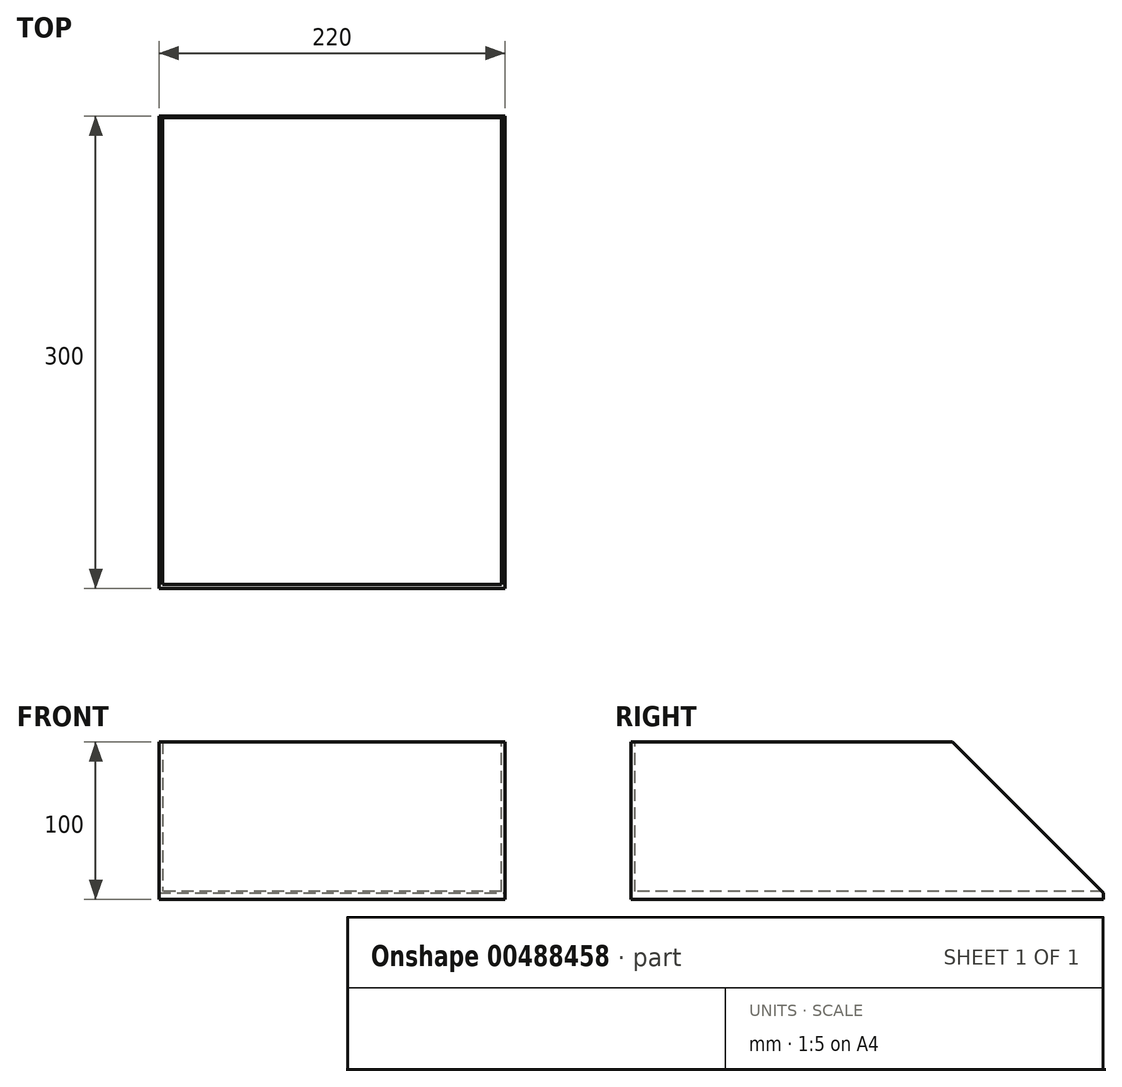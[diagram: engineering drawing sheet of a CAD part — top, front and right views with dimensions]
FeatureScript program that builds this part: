
annotation { "Feature Type Name" : "Feature", "Feature Type Description" : "" }
export const myFeature = defineFeature(function(context is Context, id is Id, definition is map)
    precondition{}
    {
        {
            var Q0;
            Q0=qCreatedBy(makeId("Top.planeOp"),FACE);
            var sketch = newSketch(context, id + "F0", { "sketchPlane" : qUnion([Q0])});
            skLineSegment(sketch, "E0.bottom", {"start": v(-110, 150) * mm, "end": v(110, 150) * mm});
            skLineSegment(sketch, "E0.top", {"start": v(-110, -150) * mm, "end": v(110, -150) * mm});
            skLineSegment(sketch, "E0.left", {"start": v(-110, 150) * mm, "end": v(-110, -150) * mm});
            skLineSegment(sketch, "E0.right", {"start": v(110, 150) * mm, "end": v(110, -150) * mm});
            skPoint(sketch, "E0.middle", {"position": v(0, 0) * mm});
            skSolve(sketch);
        }
        {
            var Q0;
            Q0=makeQuery(id+"F0.imprint","IMPRINT",FACE,{"disambiguationData":[TD([[makeQuery(id+"F0.imprint","IMPRINT",EDGE,{"derivedFrom":sQuery(id+"F0.wireOp",EDGE,"E0.bottom")}),-1.0]])]});
            extrude(context, id + "F1", {"entities" : qUnion([Q0]), "depth" : 100 * mm});
        }
        {
            var Q0;
            Q0=makeQuery(id+"F1.opExtrude","CAP_FACE",FACE,{"disambiguationData":[OSD([sQuery(id+"F0.wireOp",EDGE,"E0.bottom"),sQuery(id+"F0.wireOp",EDGE,"E0.top"),sQuery(id+"F0.wireOp",EDGE,"E0.left"),sQuery(id+"F0.wireOp",EDGE,"E0.right")])],"isStart":false});
            var sketch = newSketch(context, id + "F2", { "sketchPlane" : qUnion([Q0])});
            skLineSegment(sketch, "E1.bottom", {"start": v(107.5, 147.5) * mm, "end": v(-107.5, 147.5) * mm});
            skLineSegment(sketch, "E1.top", {"start": v(107.5, -147.5) * mm, "end": v(-107.5, -147.5) * mm});
            skLineSegment(sketch, "E1.left", {"start": v(107.5, 147.5) * mm, "end": v(107.5, -147.5) * mm});
            skLineSegment(sketch, "E1.right", {"start": v(-107.5, 147.5) * mm, "end": v(-107.5, -147.5) * mm});
            skPoint(sketch, "E1.middle", {"position": v(0, 0) * mm});
            skSolve(sketch);
        }
        {
            var Q0;
            Q0=makeQuery(id+"F2.imprint","IMPRINT",FACE,{"disambiguationData":[TD([[makeQuery(id+"F2.imprint","IMPRINT",EDGE,{"derivedFrom":sQuery(id+"F2.wireOp",EDGE,"E1.bottom")}),1.0]])]});
            extrude(context, id + "F3", {"entities" : qUnion([Q0]), "operationType" : NewBodyOperationType.REMOVE, "oppositeDirection" : true, "depth" : 95 * mm});
        }
        {
            var Q0;
            Q0=makeQuery(id+"F3.boolean.opBoolean","COPY",FACE,{"derivedFrom":makeQuery(id+"F3.opExtrude","SWEPT_FACE",FACE,{"disambiguationData":[OSD([sQuery(id+"F2.wireOp",EDGE,"E1.bottom")])]})});
            var sketch = newSketch(context, id + "F4", { "sketchPlane" : qUnion([Q0])});
            skLineSegment(sketch, "E2.bottom", {"start": v(-107.5, 100) * mm, "end": v(107.5, 100) * mm});
            skLineSegment(sketch, "E2.top", {"start": v(-107.5, 5) * mm, "end": v(107.5, 5) * mm});
            skLineSegment(sketch, "E2.left", {"start": v(-107.5, 100) * mm, "end": v(-107.5, 5) * mm});
            skLineSegment(sketch, "E2.right", {"start": v(107.5, 100) * mm, "end": v(107.5, 5) * mm});
            skSolve(sketch);
        }
        {
            var Q0;
            Q0=makeQuery(id+"F4.imprint","IMPRINT",FACE,{"disambiguationData":[TD([[makeQuery(id+"F4.imprint","IMPRINT",EDGE,{"derivedFrom":sQuery(id+"F4.wireOp",EDGE,"E2.bottom")}),1.0]])]});
            extrude(context, id + "F5", {"entities" : qUnion([Q0]), "operationType" : NewBodyOperationType.REMOVE, "oppositeDirection" : true, "depth" : 5 * mm});
        }
        {
            var Q0;
            {var subQ0=sQuery(id+"F0.wireOp",EDGE,"E0.left");var subQ1=sQuery(id+"F0.wireOp",EDGE,"E0.bottom");Q0=makeQuery(id+"F5.boolean.opBoolean","SPLIT",EDGE,{"disambiguationData":[TD([makeQuery(id+"F1.opExtrude","SWEPT_FACE",FACE,{"disambiguationData":[OSD([subQ0])]})])],"derivedFrom":makeQuery(id+"F1.opExtrude","CAP_EDGE",EDGE,{"disambiguationData":[OSD([subQ1])],"isStart":false})});}
            chamfer(context, id + "F6", {"entities" : qUnion([Q0]), "width" : 96 * mm, "tangentPropagation" : true});
        }
    });
